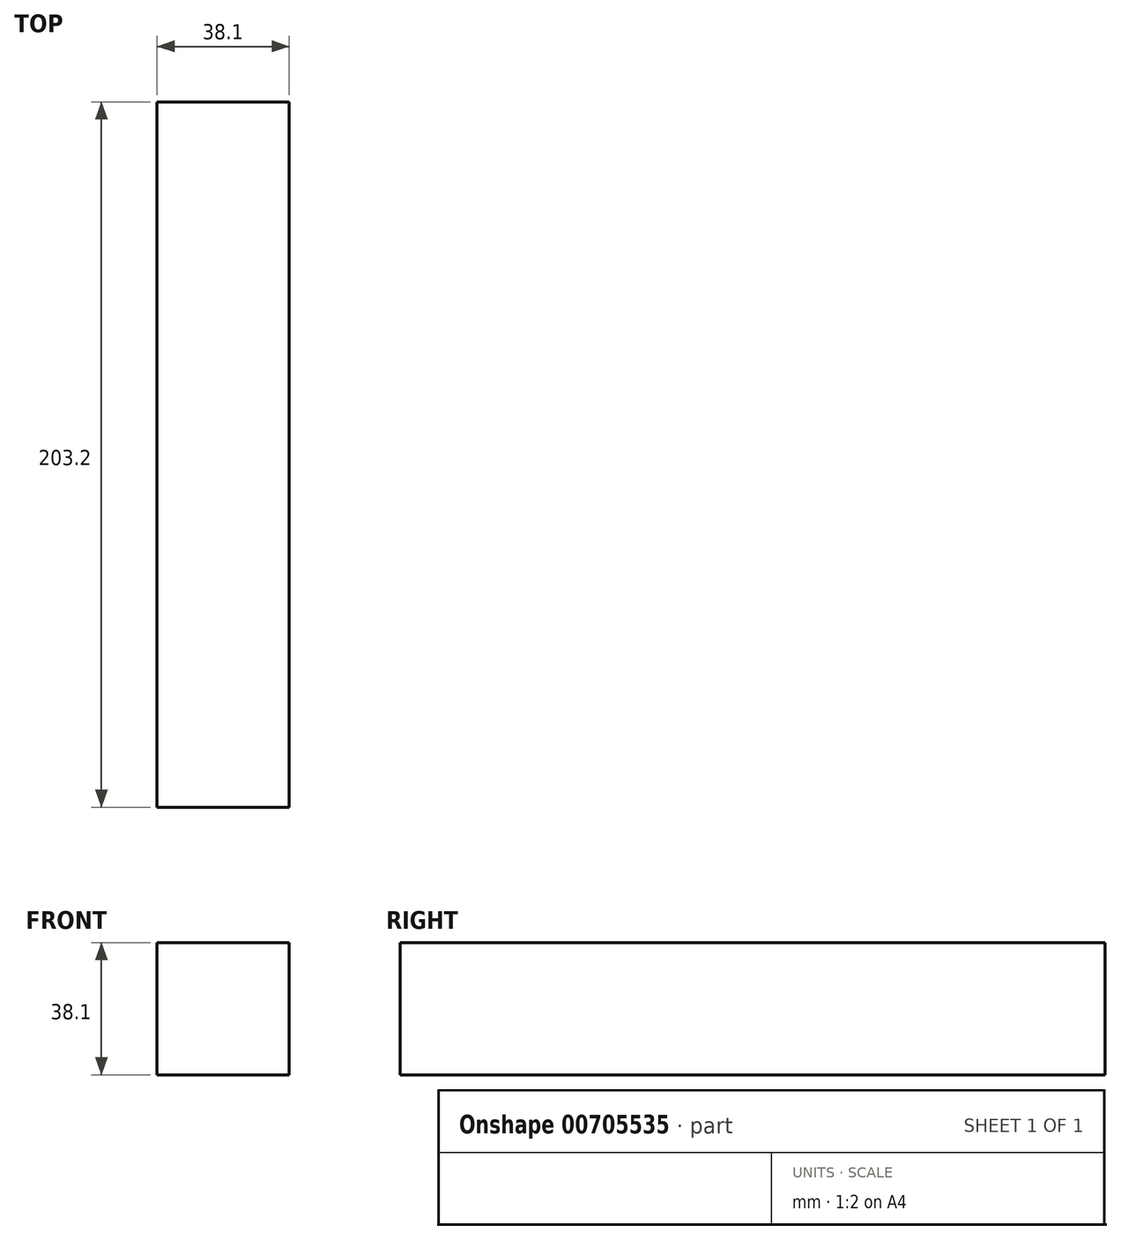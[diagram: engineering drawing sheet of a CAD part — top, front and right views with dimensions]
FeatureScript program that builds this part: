
annotation { "Feature Type Name" : "Feature", "Feature Type Description" : "" }
export const myFeature = defineFeature(function(context is Context, id is Id, definition is map)
    precondition{}
    {
        {
            var Q0;
            Q0=qCreatedBy(makeId("Front.planeOp"),FACE);
            var sketch = newSketch(context, id + "F0", { "sketchPlane" : qUnion([Q0])});
            skLineSegment(sketch, "E0.bottom", {"start": v(-60.14, 28.45) * mm, "end": v(-22.04, 28.45) * mm});
            skLineSegment(sketch, "E0.top", {"start": v(-60.14, -9.65) * mm, "end": v(-22.04, -9.65) * mm});
            skLineSegment(sketch, "E0.left", {"start": v(-60.14, 28.45) * mm, "end": v(-60.14, -9.65) * mm});
            skLineSegment(sketch, "E0.right", {"start": v(-22.04, 28.45) * mm, "end": v(-22.04, -9.65) * mm});
            skSolve(sketch);
        }
        {
            var Q0;
            Q0 = qSketchRegion(id + "F0", true);
            extrude(context, id + "F1", {"entities" : qUnion([Q0]), "depth" : 203.2 * mm, "offsetDistance" : 25.4 * mm});
        }
    });
